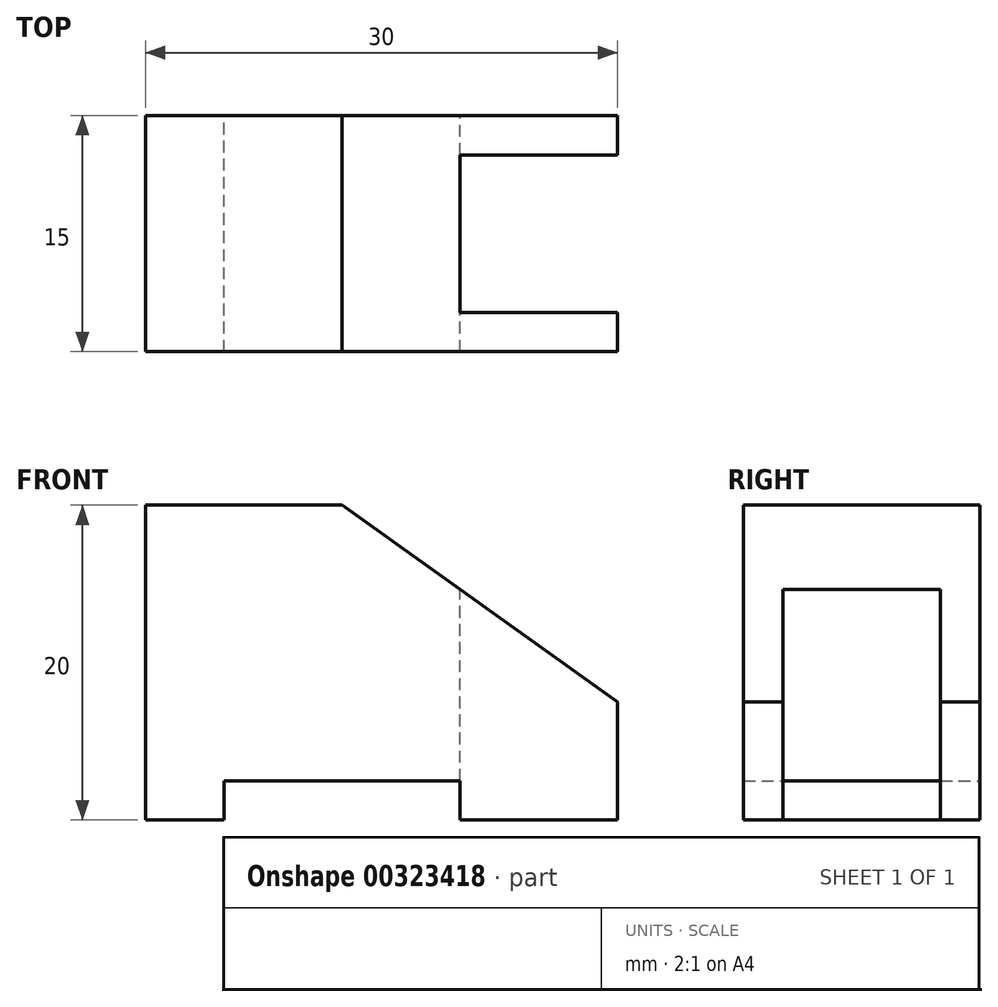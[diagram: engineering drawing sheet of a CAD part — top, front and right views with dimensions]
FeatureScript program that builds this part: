
annotation { "Feature Type Name" : "Feature", "Feature Type Description" : "" }
export const myFeature = defineFeature(function(context is Context, id is Id, definition is map)
    precondition{}
    {
        {
            var Q0;
            Q0=qCreatedBy(makeId("Front.planeOp"),FACE);
            var sketch = newSketch(context, id + "F0", { "sketchPlane" : qUnion([Q0])});
            skLineSegment(sketch, "E0", {"start": v(0, 0) * mm, "end": v(0, 20) * mm});
            skLineSegment(sketch, "E1", {"start": v(0, 20) * mm, "end": v(12.5, 20) * mm});
            skLineSegment(sketch, "E2", {"start": v(12.5, 20) * mm, "end": v(30, 7.5) * mm});
            skLineSegment(sketch, "E3", {"start": v(30, 7.5) * mm, "end": v(30, 0) * mm});
            skLineSegment(sketch, "E4", {"start": v(30, 0) * mm, "end": v(20, 0) * mm});
            skLineSegment(sketch, "E5", {"start": v(20, 0) * mm, "end": v(20, 2.5) * mm});
            skLineSegment(sketch, "E6", {"start": v(20, 2.5) * mm, "end": v(5, 2.5) * mm});
            skLineSegment(sketch, "E7", {"start": v(5, 2.5) * mm, "end": v(5, 0) * mm});
            skLineSegment(sketch, "E8", {"start": v(5, 0) * mm, "end": v(0, 0) * mm});
            skSolve(sketch);
        }
        {
            var Q0;
            Q0=makeQuery(id+"F0.imprint","IMPRINT",FACE,{"disambiguationData":[TD([[makeQuery(id+"F0.imprint","IMPRINT",EDGE,{"derivedFrom":sQuery(id+"F0.wireOp",EDGE,"E0")}),-1.0]])]});
            extrude(context, id + "F1", {"entities" : qUnion([Q0]), "depth" : 15 * mm, "symmetric" : true});
        }
        {
            var Q0;
            Q0=makeQuery(id+"F1.opExtrude","SWEPT_FACE",FACE,{"disambiguationData":[OSD([sQuery(id+"F0.wireOp",EDGE,"E1")])]});
            var sketch = newSketch(context, id + "F2", { "sketchPlane" : qUnion([Q0])});
            skLineSegment(sketch, "E9.0", {"start": v(12.5, 7.5) * mm, "end": v(30, 7.5) * mm});
            skLineSegment(sketch, "E10.0", {"start": v(30, -7.5) * mm, "end": v(30, 7.5) * mm});
            skLineSegment(sketch, "E11.0", {"start": v(12.5, -7.5) * mm, "end": v(30, -7.5) * mm});
            skLineSegment(sketch, "E12.0", {"start": v(12.5, -7.5) * mm, "end": v(12.5, 7.5) * mm});
            skLineSegment(sketch, "E13", {"start": v(30, 5) * mm, "end": v(20, 5) * mm});
            skLineSegment(sketch, "E14", {"start": v(20, 5) * mm, "end": v(20, -5) * mm});
            skLineSegment(sketch, "E15", {"start": v(20, -5) * mm, "end": v(30, -5) * mm});
            skSolve(sketch);
        }
        {
            var Q0;
            {var subQ0=sQuery(id+"F2.wireOp",EDGE,"E13");Q0=makeQuery(id+"F2.imprint","IMPRINT",FACE,{"disambiguationData":[TD([[makeQuery(id+"F2.imprint","IMPRINT",EDGE,{"derivedFrom":subQ0}),1.0]])]});}
            extrude(context, id + "F3", {"entities" : qUnion([Q0]), "operationType" : NewBodyOperationType.REMOVE, "endBound" : BoundingType.THROUGH_ALL, "oppositeDirection" : true, "depth" : 25 * mm});
        }
    });
